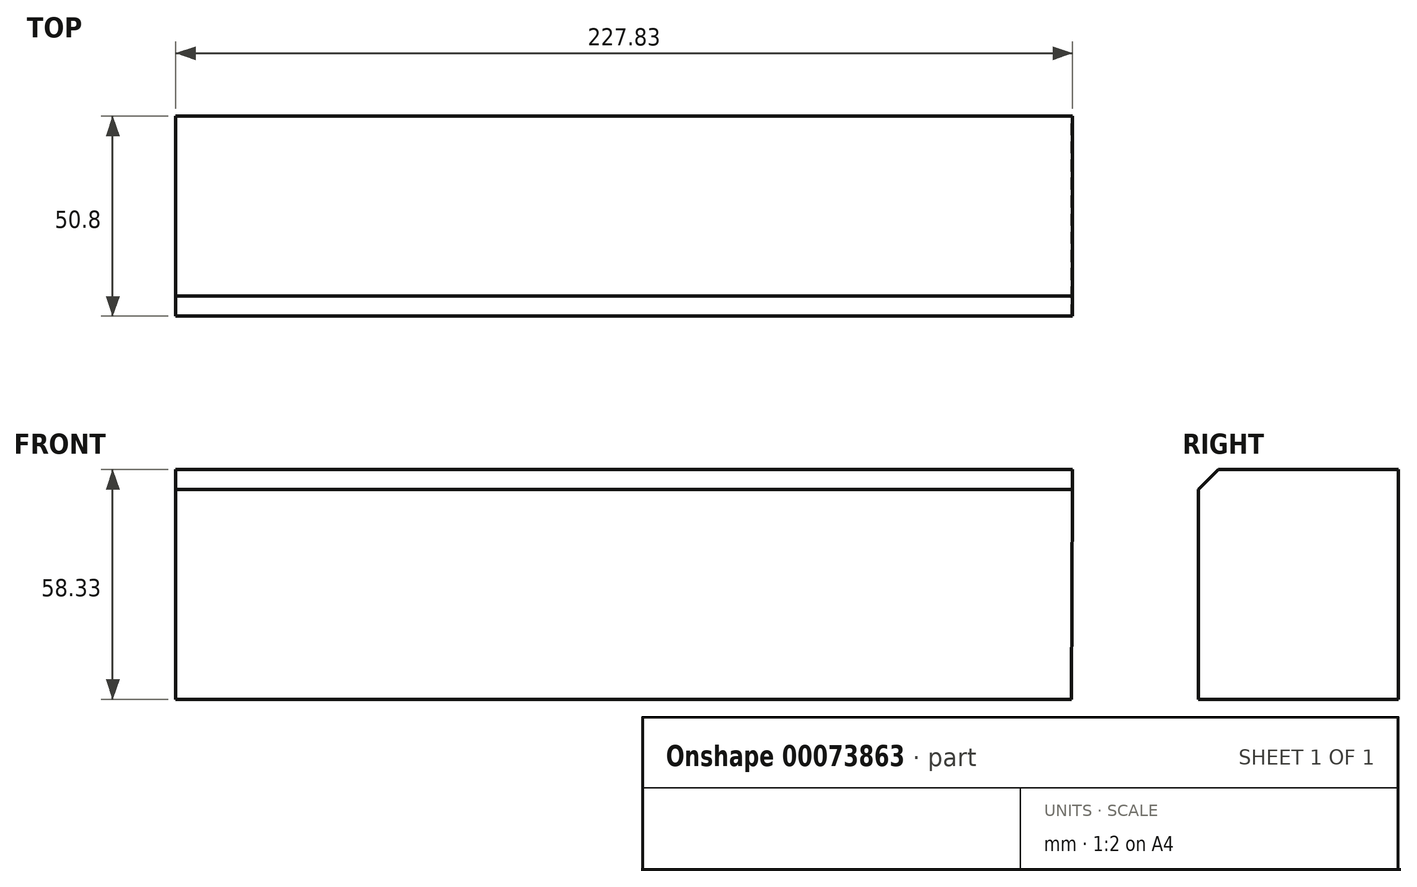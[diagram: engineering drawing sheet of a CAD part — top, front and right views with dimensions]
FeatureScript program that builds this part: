
annotation { "Feature Type Name" : "Feature", "Feature Type Description" : "" }
export const myFeature = defineFeature(function(context is Context, id is Id, definition is map)
    precondition{}
    {
        {
            var Q0;
            Q0=qCreatedBy(makeId("Front.planeOp"),FACE);
            var sketch = newSketch(context, id + "F0", { "sketchPlane" : qUnion([Q0])});
            skLineSegment(sketch, "E0", {"start": v(-116.65, -30.27) * mm, "end": v(110.9, -30.27) * mm});
            skLineSegment(sketch, "E1", {"start": v(-116.65, -30.27) * mm, "end": v(-116.65, 28.06) * mm});
            skLineSegment(sketch, "E2", {"start": v(-116.65, 28.06) * mm, "end": v(111.18, 28.06) * mm});
            skLineSegment(sketch, "E3", {"start": v(111.18, 28.06) * mm, "end": v(110.9, -30.27) * mm});
            skSolve(sketch);
        }
        {
            var Q0;
            Q0 = qSketchRegion(id + "F0", true);
            extrude(context, id + "F1", {"entities" : qUnion([Q0]), "depth" : 50.8 * mm});
        }
        {
            var Q0;
            Q0=makeQuery(id+"F1.opExtrude","CAP_EDGE",EDGE,{"disambiguationData":[OSD([sQuery(id+"F0.wireOp",EDGE,"E2")])],"isStart":false});
            chamfer(context, id + "F2", {"entities" : qUnion([Q0]), "width" : 5.08 * mm, "tangentPropagation" : true});
        }
    });
